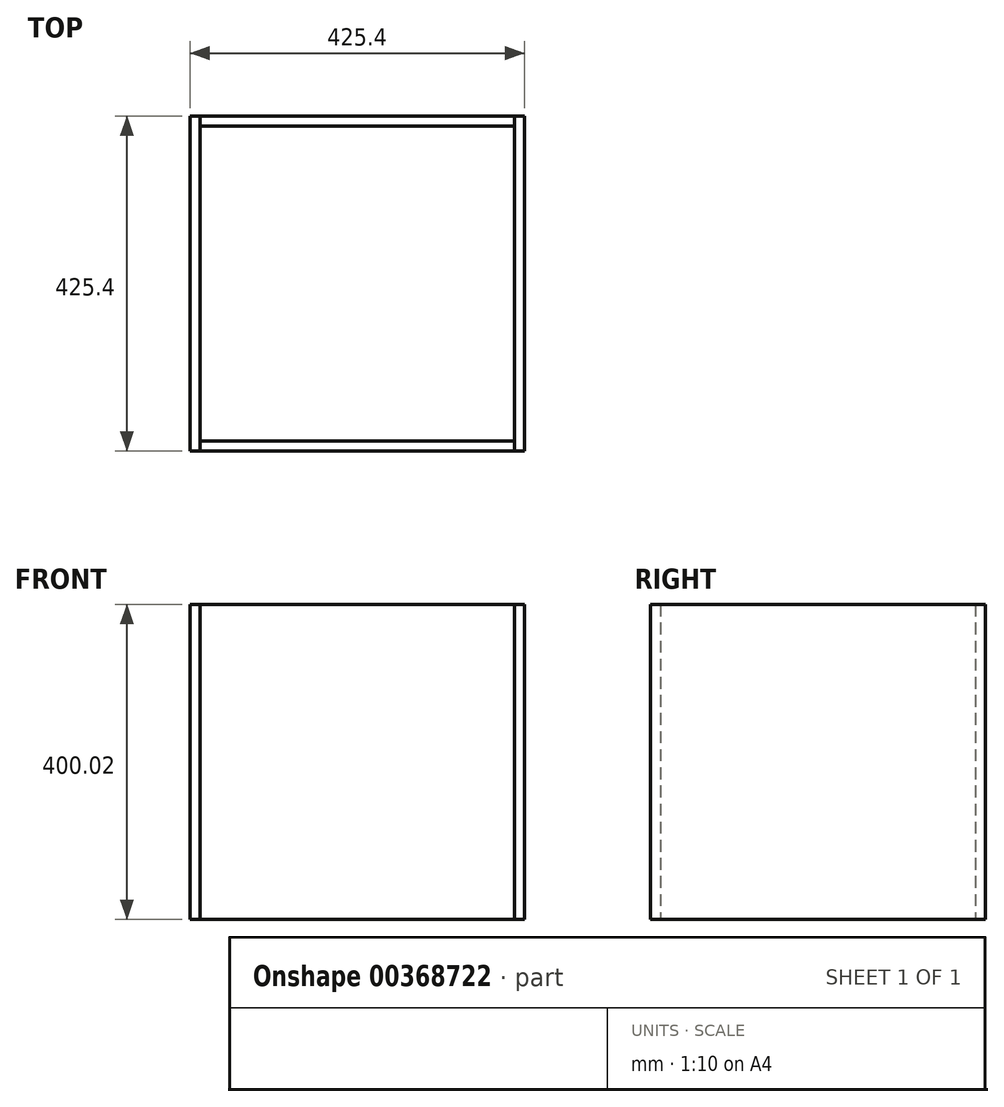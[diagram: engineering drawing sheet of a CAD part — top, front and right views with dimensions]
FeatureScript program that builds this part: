
annotation { "Feature Type Name" : "Feature", "Feature Type Description" : "" }
export const myFeature = defineFeature(function(context is Context, id is Id, definition is map)
    precondition{}
    {
        {
            var Q0;
            Q0=qCreatedBy(makeId("Top.planeOp"),FACE);
            var sketch = newSketch(context, id + "F0", { "sketchPlane" : qUnion([Q0])});
            skLineSegment(sketch, "E0.bottom", {"start": v(200, 200) * mm, "end": v(-200, 200) * mm});
            skLineSegment(sketch, "E0.top", {"start": v(200, -200) * mm, "end": v(-200, -200) * mm});
            skLineSegment(sketch, "E0.left", {"start": v(200, 200) * mm, "end": v(200, -200) * mm});
            skLineSegment(sketch, "E0.right", {"start": v(-200, 200) * mm, "end": v(-200, -200) * mm});
            skPoint(sketch, "E0.middle", {"position": v(0, 0) * mm});
            skLineSegment(sketch, "E1.bottom", {"start": v(212.7, 212.7) * mm, "end": v(-212.7, 212.7) * mm});
            skLineSegment(sketch, "E1.top", {"start": v(212.7, -212.7) * mm, "end": v(-212.7, -212.7) * mm});
            skLineSegment(sketch, "E1.left", {"start": v(212.7, 212.7) * mm, "end": v(212.7, -212.7) * mm});
            skLineSegment(sketch, "E1.right", {"start": v(-212.7, 212.7) * mm, "end": v(-212.7, -212.7) * mm});
            skLineSegment(sketch, "E2", {"start": v(-200, 200) * mm, "end": v(-200, 212.7) * mm});
            skLineSegment(sketch, "E3", {"start": v(-200, 212.7) * mm, "end": v(200, 212.7) * mm});
            skLineSegment(sketch, "E4", {"start": v(200, 212.7) * mm, "end": v(200, 200) * mm});
            skLineSegment(sketch, "E5", {"start": v(200, -212.7) * mm, "end": v(200, -200) * mm});
            skLineSegment(sketch, "E6", {"start": v(-200, -200) * mm, "end": v(-200, -212.7) * mm});
            skSolve(sketch);
        }
        {
            var Q0;
            Q0=makeQuery(id+"F0.imprint","IMPRINT",FACE,{"disambiguationData":[TD([[makeQuery(id+"F0.imprint","IMPRINT",EDGE,{"derivedFrom":sQuery(id+"F0.wireOp",EDGE,"E0.bottom")}),1.0]])]});
            var Q1;
            Q1=makeQuery(id+"F0.imprint","IMPRINT",FACE,{"disambiguationData":[TD([[makeQuery(id+"F0.imprint","IMPRINT",EDGE,{"derivedFrom":sQuery(id+"F0.wireOp",EDGE,"E0.top")}),1.0]])]});
            var Q2;
            Q2=makeQuery(id+"F0.imprint","IMPRINT",FACE,{"disambiguationData":[TD([[makeQuery(id+"F0.imprint","IMPRINT",EDGE,{"derivedFrom":sQuery(id+"F0.wireOp",EDGE,"E0.left")}),1.0]])]});
            var Q3;
            Q3=makeQuery(id+"F0.imprint","IMPRINT",FACE,{"disambiguationData":[TD([[makeQuery(id+"F0.imprint","IMPRINT",EDGE,{"derivedFrom":sQuery(id+"F0.wireOp",EDGE,"E0.bottom")}),-1.0]])]});
            var Q4;
            Q4=makeQuery(id+"F0.imprint","IMPRINT",FACE,{"disambiguationData":[TD([[makeQuery(id+"F0.imprint","IMPRINT",EDGE,{"derivedFrom":sQuery(id+"F0.wireOp",EDGE,"E0.right")}),-1.0]])]});
            extrude(context, id + "F1", {"entities" : qUnion([Q0, Q1, Q2, Q3, Q4]), "oppositeDirection" : true, "depth" : 1 / 50.8 * mm});
        }
        {
            var Q0;
            Q0=makeQuery(id+"F0.imprint","IMPRINT",FACE,{"disambiguationData":[TD([[makeQuery(id+"F0.imprint","IMPRINT",EDGE,{"derivedFrom":sQuery(id+"F0.wireOp",EDGE,"E0.right")}),-1.0]])]});
            extrude(context, id + "F2", {"entities" : qUnion([Q0]), "depth" : 400 * mm});
        }
        {
            var Q0;
            Q0=makeQuery(id+"F0.imprint","IMPRINT",FACE,{"disambiguationData":[TD([[makeQuery(id+"F0.imprint","IMPRINT",EDGE,{"derivedFrom":sQuery(id+"F0.wireOp",EDGE,"E0.bottom")}),-1.0]])]});
            extrude(context, id + "F3", {"entities" : qUnion([Q0]), "depth" : 400 * mm});
        }
        {
            var Q0;
            Q0=makeQuery(id+"F0.imprint","IMPRINT",FACE,{"disambiguationData":[TD([[makeQuery(id+"F0.imprint","IMPRINT",EDGE,{"derivedFrom":sQuery(id+"F0.wireOp",EDGE,"E0.left")}),1.0]])]});
            extrude(context, id + "F4", {"entities" : qUnion([Q0]), "depth" : 400 * mm});
        }
        {
            var Q0;
            Q0=makeQuery(id+"F0.imprint","IMPRINT",FACE,{"disambiguationData":[TD([[makeQuery(id+"F0.imprint","IMPRINT",EDGE,{"derivedFrom":sQuery(id+"F0.wireOp",EDGE,"E0.top")}),1.0]])]});
            extrude(context, id + "F5", {"entities" : qUnion([Q0]), "depth" : 400 * mm});
        }
    });
